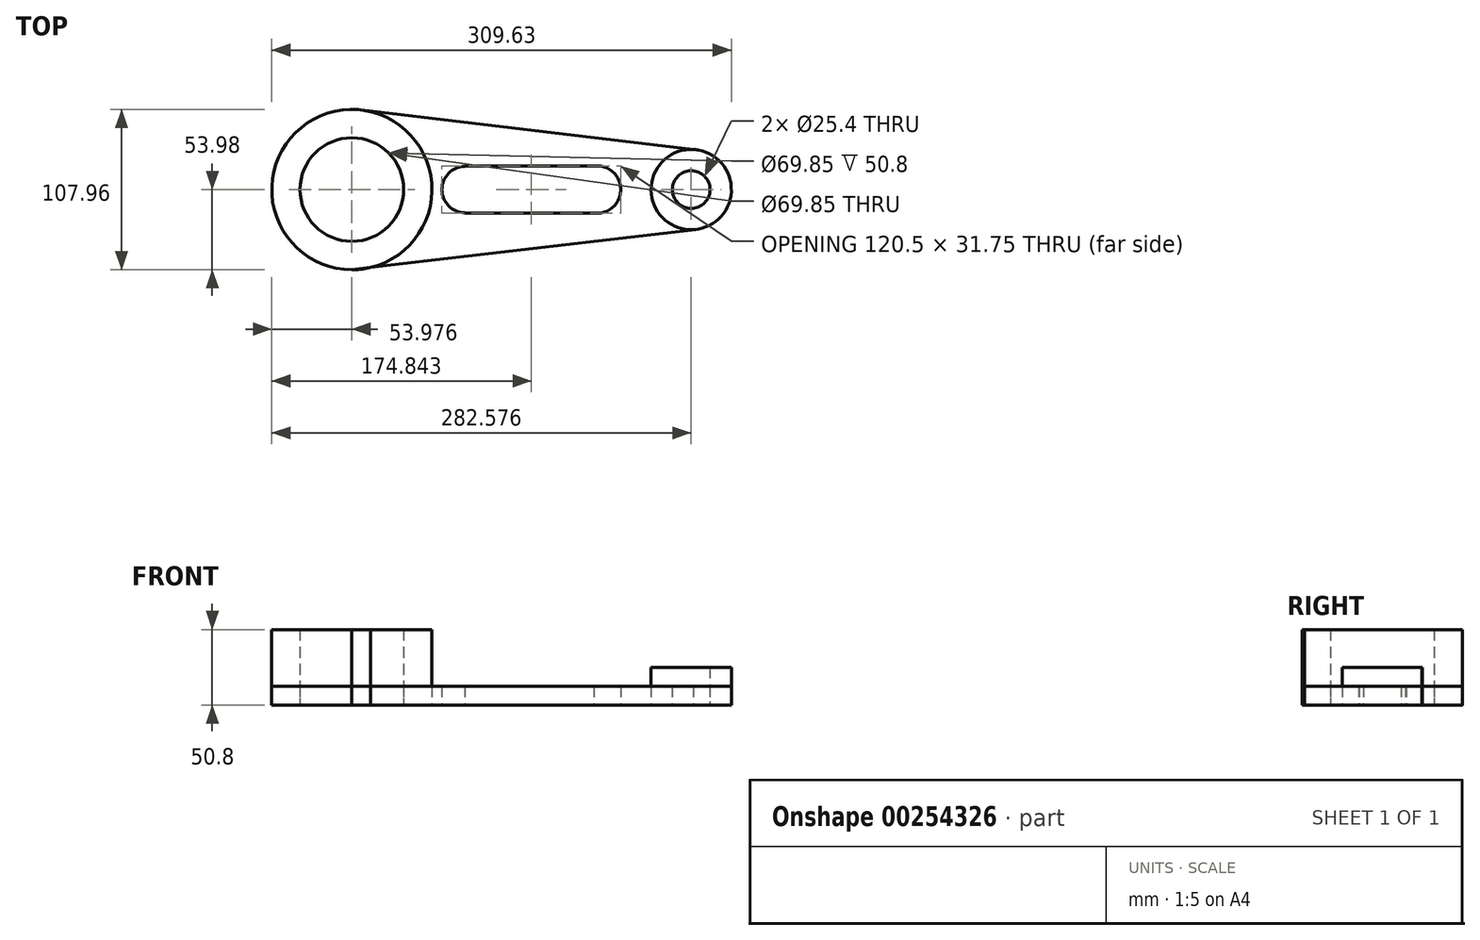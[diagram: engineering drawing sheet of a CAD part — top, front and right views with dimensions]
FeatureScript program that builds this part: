
annotation { "Feature Type Name" : "Feature", "Feature Type Description" : "" }
export const myFeature = defineFeature(function(context is Context, id is Id, definition is map)
    precondition{}
    {
        {
            var Q0;
            Q0=qCreatedBy(makeId("Top.planeOp"),FACE);
            var sketch = newSketch(context, id + "F0", { "sketchPlane" : qUnion([Q0])});
            skCircle(sketch, "E0", {"center": v(-101.47, 0) * mm, "radius": 34.93 * mm});
            skCircle(sketch, "E1", {"center": v(-101.47, 0) * mm, "radius": 53.98 * mm});
            skCircle(sketch, "E2", {"center": v(127.13, 0) * mm, "radius": 12.7 * mm});
            skCircle(sketch, "E3", {"center": v(127.13, 0) * mm, "radius": 27.05 * mm});
            skLineSegment(sketch, "E4.bottom", {"start": v(63.63, -15.87) * mm, "end": v(-25.27, -15.88) * mm});
            skLineSegment(sketch, "E4.top", {"start": v(63.63, 15.88) * mm, "end": v(-25.27, 15.88) * mm});
            skLineSegment(sketch, "E4.right", {"start": v(-25.27, -15.88) * mm, "end": v(-25.27, -15.58) * mm});
            skPoint(sketch, "E4.middle", {"position": v(19.18, 0) * mm});
            skArc(sketch, "E5", {"start": v(-25.27, 15.58) * mm, "mid": v(-40.86, 0) * mm, "end": v(-25.27, -15.58) * mm});
            skArc(sketch, "E6", {"start": v(61.5, -15.87) * mm, "mid": v(79.64, 0) * mm, "end": v(61.5, 15.88) * mm});
            skLineSegment(sketch, "E7.trimOffspring", {"start": v(-25.27, 15.58) * mm, "end": v(-25.27, 15.88) * mm});
            skLineSegment(sketch, "E8.left", {"start": v(-101.47, -53.98) * mm, "end": v(-101.47, -54.22) * mm});
            skLineSegment(sketch, "E9", {"start": v(-95.1, 53.6) * mm, "end": v(131.9, 26.63) * mm});
            skLineSegment(sketch, "E10", {"start": v(-101.47, -53.98) * mm, "end": v(130.27, -26.87) * mm});
            skSolve(sketch);
        }
        {
            var Q0;
            Q0=makeQuery(id+"F0.imprint","IMPRINT",FACE,{"disambiguationData":[TD([[makeQuery(id+"F0.imprint","IMPRINT",EDGE,{"derivedFrom":sQuery(id+"F0.wireOp",EDGE,"E2")}),-1.0]])]});
            extrude(context, id + "F1", {"entities" : qUnion([Q0]), "depth" : 25.4 * mm});
        }
        {
            var Q0;
            Q0=makeQuery(id+"F0.imprint","IMPRINT",FACE,{"disambiguationData":[TD([[makeQuery(id+"F0.imprint","IMPRINT",EDGE,{"derivedFrom":sQuery(id+"F0.wireOp",EDGE,"E0")}),-1.0]])]});
            var Q1;
            Q1=sQuery(id+"F0.wireOp",EDGE,"tahW8BBD-pPEN-1MDB-NpQo-0CSrbzv319cd");
            var Q2;
            Q2=sQuery(id+"F0.wireOp",EDGE,"HG2BkS8G-hP0H-nPKz-sEMY-PAIBukyAU6Nj");
            extrude(context, id + "F2", {"entities" : qUnion([Q0]), "surfaceEntities" : qUnion([Q1, Q2]), "depth" : 50.8 * mm});
        }
        {
            var Q0;
            Q0 = qSketchRegion(id + "F0", true);
            extrude(context, id + "F3", {"entities" : qUnion([Q0]), "depth" : 12.7 * mm});
        }
    });
